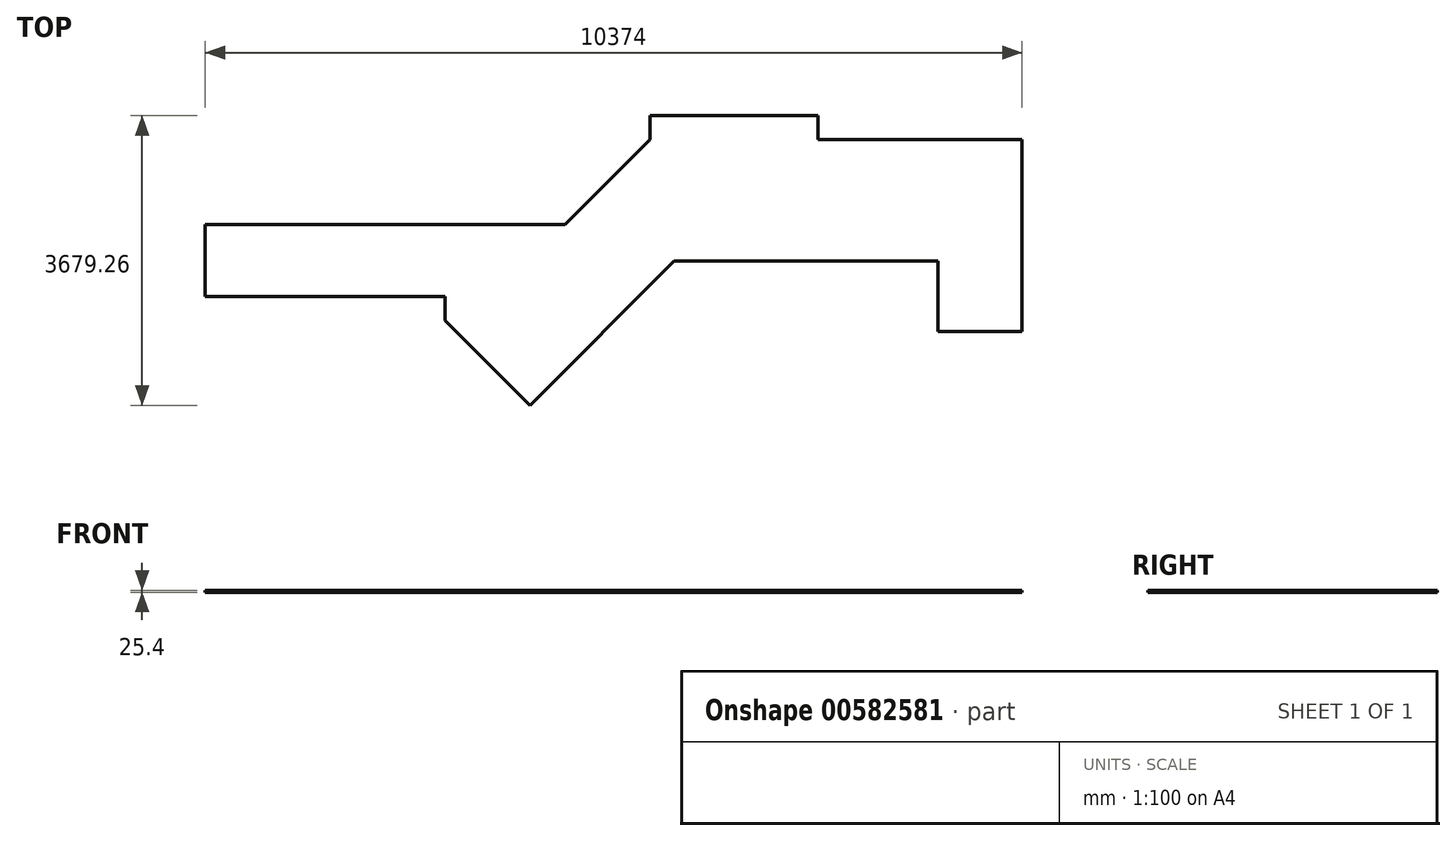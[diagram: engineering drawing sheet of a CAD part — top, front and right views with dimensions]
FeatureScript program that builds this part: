
annotation { "Feature Type Name" : "Feature", "Feature Type Description" : "" }
export const myFeature = defineFeature(function(context is Context, id is Id, definition is map)
    precondition{}
    {
        {
            var Q0;
            Q0=qCreatedBy(makeId("Top.planeOp"),FACE);
            var sketch = newSketch(context, id + "F0", { "sketchPlane" : qUnion([Q0])});
            skLineSegment(sketch, "E0", {"start": v(0, 0) * mm, "end": v(1066.8, 0) * mm});
            skLineSegment(sketch, "E1", {"start": v(1066.8, 0) * mm, "end": v(1066.8, 2438.4) * mm});
            skLineSegment(sketch, "E2", {"start": v(1066.8, 2438.4) * mm, "end": v(-1524, 2438.4) * mm});
            skLineSegment(sketch, "E3", {"start": v(-1524, 2438.4) * mm, "end": v(-1524, 2743.2) * mm});
            skLineSegment(sketch, "E4", {"start": v(-1524, 2743.2) * mm, "end": v(-3657.6, 2743.2) * mm});
            skLineSegment(sketch, "E5", {"start": v(-3657.6, 2743.2) * mm, "end": v(-3657.6, 2438.4) * mm});
            skLineSegment(sketch, "E6", {"start": v(-3657.6, 2438.4) * mm, "end": v(-4735.23, 1360.77) * mm});
            skLineSegment(sketch, "E7", {"start": v(-4735.23, 1360.77) * mm, "end": v(-9307.23, 1360.77) * mm});
            skLineSegment(sketch, "E8", {"start": v(-9307.23, 1360.77) * mm, "end": v(-9307.23, 446.37) * mm});
            skLineSegment(sketch, "E9", {"start": v(-9307.23, 446.37) * mm, "end": v(-6259.23, 446.37) * mm});
            skLineSegment(sketch, "E10", {"start": v(-6259.23, 446.37) * mm, "end": v(-6259.23, 141.57) * mm});
            skLineSegment(sketch, "E11", {"start": v(-6259.23, 141.57) * mm, "end": v(-5181.6, -936.06) * mm});
            skLineSegment(sketch, "E12", {"start": v(-5181.6, -936.06) * mm, "end": v(-3349.63, 895.91) * mm});
            skLineSegment(sketch, "E13", {"start": v(-3349.63, 895.91) * mm, "end": v(0, 895.91) * mm});
            skLineSegment(sketch, "E14", {"start": v(0, 0) * mm, "end": v(0, 895.91) * mm});
            skSolve(sketch);
        }
        {
            var Q0;
            Q0=makeQuery(id+"F0.imprint","IMPRINT",FACE,{"disambiguationData":[TD([[makeQuery(id+"F0.imprint","IMPRINT",EDGE,{"derivedFrom":sQuery(id+"F0.wireOp",EDGE,"E0")}),1.0]])]});
            extrude(context, id + "F1", {"entities" : qUnion([Q0]), "depth" : 25.4 * mm, "offsetDistance" : 25.4 * mm});
        }
    });
